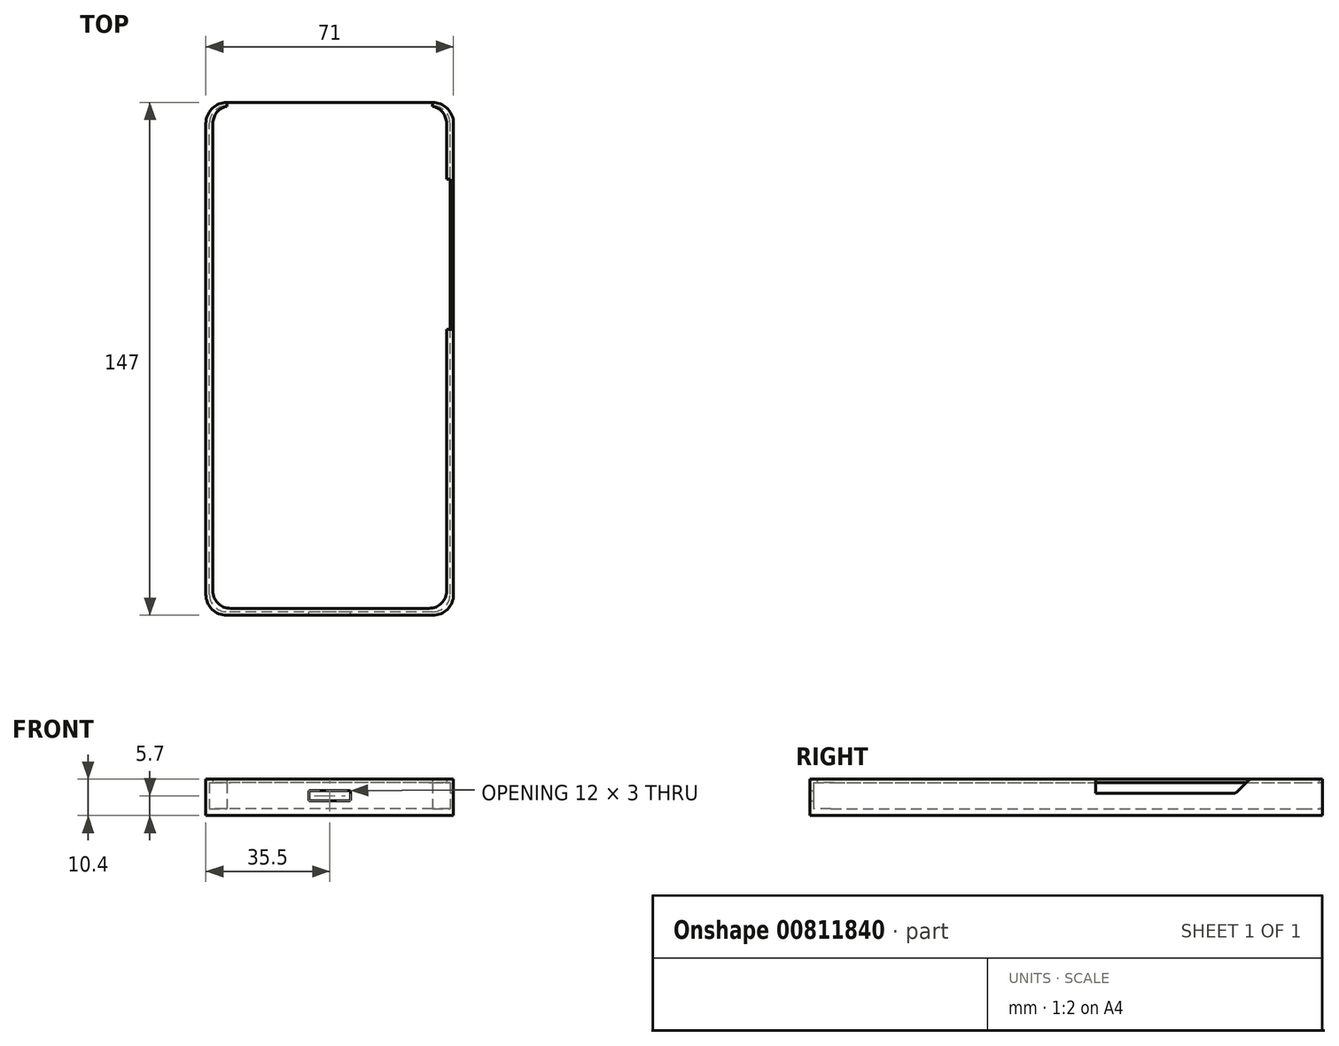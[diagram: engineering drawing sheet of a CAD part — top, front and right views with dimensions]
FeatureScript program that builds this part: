
annotation { "Feature Type Name" : "Feature", "Feature Type Description" : "" }
export const myFeature = defineFeature(function(context is Context, id is Id, definition is map)
    precondition{}
    {
        {
            var Q0;
            Q0=qCreatedBy(makeId("Top.planeOp"),FACE);
            var sketch = newSketch(context, id + "F0", { "sketchPlane" : qUnion([Q0])});
            skLineSegment(sketch, "E0.bottom", {"start": v(29.5, -72.5) * mm, "end": v(-29.5, -72.5) * mm});
            skLineSegment(sketch, "E0.top", {"start": v(29.5, 72.5) * mm, "end": v(-29.5, 72.5) * mm});
            skLineSegment(sketch, "E0.left", {"start": v(34.5, -67.5) * mm, "end": v(34.5, 67.5) * mm});
            skLineSegment(sketch, "E0.right", {"start": v(-34.5, -67.5) * mm, "end": v(-34.5, 67.5) * mm});
            skPoint(sketch, "E0.middle", {"position": v(0, 0) * mm});
            skLineSegment(sketch, "E1.bottom", {"start": v(29.5, -73.5) * mm, "end": v(-29.5, -73.5) * mm});
            skLineSegment(sketch, "E1.top", {"start": v(29.5, 73.5) * mm, "end": v(-29.5, 73.5) * mm});
            skLineSegment(sketch, "E1.left", {"start": v(35.5, -67.5) * mm, "end": v(35.5, 67.5) * mm});
            skLineSegment(sketch, "E1.right", {"start": v(-35.5, -67.5) * mm, "end": v(-35.5, 67.5) * mm});
            skPoint(sketch, "E2.visualSharp", {"position": v(-34.5, 72.5) * mm});
            skArc(sketch, "E2.filletArc", {"start": v(-29.5, 72.5) * mm, "mid": v(-33.04, 71.04) * mm, "end": v(-34.5, 67.5) * mm});
            skPoint(sketch, "E3.visualSharp", {"position": v(-34.5, -72.5) * mm});
            skArc(sketch, "E3.filletArc", {"start": v(-34.5, -67.5) * mm, "mid": v(-33.04, -71.04) * mm, "end": v(-29.5, -72.5) * mm});
            skPoint(sketch, "E4.visualSharp", {"position": v(34.5, -72.5) * mm});
            skArc(sketch, "E4.filletArc", {"start": v(29.5, -72.5) * mm, "mid": v(33.04, -71.04) * mm, "end": v(34.5, -67.5) * mm});
            skPoint(sketch, "E5.visualSharp", {"position": v(34.5, 72.5) * mm});
            skArc(sketch, "E5.filletArc", {"start": v(34.5, 67.5) * mm, "mid": v(33.04, 71.04) * mm, "end": v(29.5, 72.5) * mm});
            skPoint(sketch, "E6.visualSharp", {"position": v(-35.5, 73.5) * mm});
            skArc(sketch, "E6.filletArc", {"start": v(-29.5, 73.5) * mm, "mid": v(-33.74, 71.74) * mm, "end": v(-35.5, 67.5) * mm});
            skPoint(sketch, "E7.visualSharp", {"position": v(-35.5, -73.5) * mm});
            skArc(sketch, "E7.filletArc", {"start": v(-35.5, -67.5) * mm, "mid": v(-33.74, -71.74) * mm, "end": v(-29.5, -73.5) * mm});
            skPoint(sketch, "E8.visualSharp", {"position": v(35.5, -73.5) * mm});
            skArc(sketch, "E8.filletArc", {"start": v(29.5, -73.5) * mm, "mid": v(33.74, -71.74) * mm, "end": v(35.5, -67.5) * mm});
            skPoint(sketch, "E9.visualSharp", {"position": v(35.5, 73.5) * mm});
            skArc(sketch, "E9.filletArc", {"start": v(35.5, 67.5) * mm, "mid": v(33.74, 71.74) * mm, "end": v(29.5, 73.5) * mm});
            skSolve(sketch);
        }
        {
            var Q0;
            Q0=makeQuery(id+"F0.imprint","IMPRINT",FACE,{"disambiguationData":[TD([[makeQuery(id+"F0.imprint","IMPRINT",EDGE,{"derivedFrom":sQuery(id+"F0.wireOp",EDGE,"E0.bottom")}),-1.0]])]});
            extrude(context, id + "F1", {"entities" : qUnion([Q0]), "depth" : 1 * mm});
        }
        {
            var Q0;
            Q0=makeQuery(id+"F0.imprint","IMPRINT",FACE,{"disambiguationData":[TD([[makeQuery(id+"F0.imprint","IMPRINT",EDGE,{"derivedFrom":sQuery(id+"F0.wireOp",EDGE,"E0.bottom")}),1.0]])]});
            extrude(context, id + "F2", {"entities" : qUnion([Q0]), "operationType" : NewBodyOperationType.ADD, "depth" : (1 + 7.4) * mm});
        }
        {
            var Q0;
            Q0=makeQuery(id+"F2.opExtrude","CAP_FACE",FACE,{"disambiguationData":[OSD([sQuery(id+"F0.wireOp",EDGE,"E0.bottom"),sQuery(id+"F0.wireOp",EDGE,"E0.top"),sQuery(id+"F0.wireOp",EDGE,"E0.left"),sQuery(id+"F0.wireOp",EDGE,"E0.right"),sQuery(id+"F0.wireOp",EDGE,"E1.bottom"),sQuery(id+"F0.wireOp",EDGE,"E1.top"),sQuery(id+"F0.wireOp",EDGE,"E1.left"),sQuery(id+"F0.wireOp",EDGE,"E1.right"),sQuery(id+"F0.wireOp",EDGE,"E2.filletArc"),sQuery(id+"F0.wireOp",EDGE,"E3.filletArc"),sQuery(id+"F0.wireOp",EDGE,"E4.filletArc"),sQuery(id+"F0.wireOp",EDGE,"E5.filletArc"),sQuery(id+"F0.wireOp",EDGE,"E6.filletArc"),sQuery(id+"F0.wireOp",EDGE,"E7.filletArc"),sQuery(id+"F0.wireOp",EDGE,"E8.filletArc"),sQuery(id+"F0.wireOp",EDGE,"E9.filletArc")])],"isStart":false});
            var sketch = newSketch(context, id + "F3", { "sketchPlane" : qUnion([Q0])});
            skLineSegment(sketch, "E10.bottom", {"start": v(28.5, -71.5) * mm, "end": v(-28.5, -71.5) * mm});
            skLineSegment(sketch, "E10.top", {"start": v(28.5, 72.5) * mm, "end": v(-28.5, 72.5) * mm});
            skLineSegment(sketch, "E10.left", {"start": v(33.5, -66.5) * mm, "end": v(33.5, 67.5) * mm});
            skLineSegment(sketch, "E10.right", {"start": v(-33.5, -66.5) * mm, "end": v(-33.5, 67.5) * mm});
            skPoint(sketch, "E10.middle", {"position": v(0, 0.5) * mm});
            skPoint(sketch, "E11.visualSharp", {"position": v(-33.5, -71.5) * mm});
            skArc(sketch, "E11.filletArc", {"start": v(-33.5, -66.5) * mm, "mid": v(-32.04, -70.04) * mm, "end": v(-28.5, -71.5) * mm});
            skPoint(sketch, "E12.visualSharp", {"position": v(33.5, -71.5) * mm});
            skArc(sketch, "E12.filletArc", {"start": v(28.5, -71.5) * mm, "mid": v(32.04, -70.04) * mm, "end": v(33.5, -66.5) * mm});
            skPoint(sketch, "E13.visualSharp", {"position": v(33.5, 72.5) * mm});
            skArc(sketch, "E13.filletArc", {"start": v(33.5, 67.5) * mm, "mid": v(32.04, 71.04) * mm, "end": v(28.5, 72.5) * mm});
            skPoint(sketch, "E14.visualSharp", {"position": v(-33.5, 72.5) * mm});
            skArc(sketch, "E14.filletArc", {"start": v(-28.5, 72.5) * mm, "mid": v(-32.04, 71.04) * mm, "end": v(-33.5, 67.5) * mm});
            skSolve(sketch);
        }
        {
            var Q0;
            Q0=makeQuery(id+"F3.imprint","IMPRINT",FACE,{"disambiguationData":[TD([[makeQuery(id+"F3.imprint","IMPRINT",EDGE,{"derivedFrom":sQuery(id+"F3.wireOp",EDGE,"E10.bottom")}),1.0]])]});
            var Q1;
            Q1=makeQuery(id+"F3.imprint","IMPRINT",FACE,{"disambiguationData":[TD([[makeQuery(id+"F3.imprint","IMPRINT",EDGE,{"derivedFrom":makeQuery(id+"F2.opExtrude","CAP_EDGE",EDGE,{"disambiguationData":[OSD([sQuery(id+"F0.wireOp",EDGE,"E0.bottom")])],"isStart":false})}),1.0]])]});
            extrude(context, id + "F4", {"entities" : qUnion([Q0, Q1]), "operationType" : NewBodyOperationType.ADD, "depth" : 1 * mm});
        }
        {
            var Q0;
            Q0=makeQuery(id+"F4.boolean.opBoolean","MERGE",FACE,{"derivedFrom":[makeQuery(id+"F2.opExtrude","SWEPT_FACE",FACE,{"disambiguationData":[OSD([sQuery(id+"F0.wireOp",EDGE,"E0.top")])]}),makeQuery(id+"F4.opExtrude","SWEPT_FACE",FACE,{"disambiguationData":[OSD([sQuery(id+"F3.wireOp",EDGE,"E10.top")])]})]});
            extrude(context, id + "F5", {"entities" : qUnion([Q0]), "operationType" : NewBodyOperationType.REMOVE, "endBound" : BoundingType.THROUGH_ALL, "oppositeDirection" : true, "depth" : 25 * mm});
        }
        {
            var Q0;
            {var subQ2=sQuery(id+"F0.wireOp",EDGE,"E0.top");var subQ3=sQuery(id+"F3.wireOp",EDGE,"E14.filletArc");var subQ9=sQuery(id+"F3.wireOp",EDGE,"E10.top");var subQ16=sQuery(id+"F0.wireOp",EDGE,"E1.top");Q0=makeQuery(id+"F5.boolean.opBoolean","SPLIT",FACE,{"disambiguationData":[TD([makeQuery(id+"F5.opExtrude","SWEPT_FACE",FACE,{"disambiguationData":[OSD([subQ2,subQ9,subQ3])]})])],"derivedFrom":makeQuery(id+"F4.boolean.opBoolean","MERGE",FACE,{"derivedFrom":[makeQuery(id+"F2.opExtrude","SWEPT_FACE",FACE,{"disambiguationData":[OSD([subQ16])]}),makeQuery(id+"F4.opExtrude","SWEPT_FACE",FACE,{"disambiguationData":[OSD([subQ16])]})]})});}
            var Q1;
            {var subQ2=sQuery(id+"F3.wireOp",EDGE,"E13.filletArc");var subQ7=sQuery(id+"F3.wireOp",EDGE,"E10.top");var subQ14=sQuery(id+"F0.wireOp",EDGE,"E1.top");var subQ17=sQuery(id+"F0.wireOp",EDGE,"E0.top");Q1=makeQuery(id+"F5.boolean.opBoolean","SPLIT",FACE,{"disambiguationData":[TD([makeQuery(id+"F5.opExtrude","SWEPT_FACE",FACE,{"disambiguationData":[OSD([subQ17,subQ7,subQ2])]})])],"derivedFrom":makeQuery(id+"F4.boolean.opBoolean","MERGE",FACE,{"derivedFrom":[makeQuery(id+"F2.opExtrude","SWEPT_FACE",FACE,{"disambiguationData":[OSD([subQ14])]}),makeQuery(id+"F4.opExtrude","SWEPT_FACE",FACE,{"disambiguationData":[OSD([subQ14])]})]})});}
            extrude(context, id + "F6", {"entities" : qUnion([Q0, Q1]), "operationType" : NewBodyOperationType.REMOVE, "endBound" : BoundingType.UP_TO_NEXT, "oppositeDirection" : true, "depth" : 25 * mm});
        }
        {
            var Q0;
            {var subQ0=sQuery(id+"F0.wireOp",EDGE,"E9.filletArc");var subQ1=sQuery(id+"F0.wireOp",EDGE,"E1.top");var subQ2=makeQuery(id+"F2.opExtrude","SWEPT_FACE",FACE,{"disambiguationData":[OSD([subQ0])]});var subQ3=makeQuery(id+"F4.opExtrude","SWEPT_FACE",FACE,{"disambiguationData":[OSD([subQ0])]});var subQ4=sQuery(id+"F0.wireOp",EDGE,"E5.filletArc");var subQ5=sQuery(id+"F0.wireOp",EDGE,"E0.top");var subQ6=makeQuery(id+"F5.opExtrude","SWEPT_FACE",FACE,{"disambiguationData":[OSD([subQ5,subQ4])]});var subQ7=makeQuery(id+"F4.boolean.opBoolean","MERGE",EDGE,{"derivedFrom":[makeQuery(id+"F2.opExtrude","SWEPT_EDGE",EDGE,{"disambiguationData":[OSD([subQ1,subQ0])]}),makeQuery(id+"F4.opExtrude","SWEPT_EDGE",EDGE,{"disambiguationData":[OSD([subQ1,subQ0])]})]});var subQ22=makeQuery(id+"F2.opExtrude","SWEPT_FACE",FACE,{"disambiguationData":[OSD([subQ1])]});var subQ24=makeQuery(id+"F4.opExtrude","SWEPT_FACE",FACE,{"disambiguationData":[OSD([subQ1])]});var subQ27=makeQuery(id+"F2.opExtrude","CAP_EDGE",EDGE,{"disambiguationData":[OSD([subQ5])],"isStart":false});Q0=makeQuery(id+"F6.boolean.opBoolean","MERGE",EDGE,{"derivedFrom":[makeQuery(id+"F5.boolean.opBoolean","SPLIT",EDGE,{"disambiguationData":[topologyDisambiguationEdgeConnected([subQ22,subQ2,subQ24,subQ3]),TD([makeQuery(id+"F5.opExtrude","SWEPT_FACE",FACE,{"disambiguationData":[OSD([subQ5]),TDD([makeQuery(id+"F4.boolean.opBoolean","SPLIT",EDGE,{"disambiguationData":[TD([makeQuery(id+"F2.opExtrude","SWEPT_FACE",FACE,{"disambiguationData":[OSD([subQ4])]})])],"derivedFrom":subQ27})])]})])],"derivedFrom":subQ7}),makeQuery(id+"F5.boolean.opBoolean","SPLIT",EDGE,{"disambiguationData":[topologyDisambiguationEdgeConnected([subQ2,subQ3,subQ6])],"derivedFrom":subQ7}),makeQuery(id+"F6.opExtrude","CAP_EDGE",EDGE,{"disambiguationData":[OSD([subQ1,subQ0])],"isStart":true})]});}
            var Q1;
            {var subQ0=sQuery(id+"F0.wireOp",EDGE,"E6.filletArc");var subQ1=sQuery(id+"F0.wireOp",EDGE,"E1.top");var subQ2=makeQuery(id+"F2.opExtrude","SWEPT_FACE",FACE,{"disambiguationData":[OSD([subQ0])]});var subQ3=sQuery(id+"F0.wireOp",EDGE,"E2.filletArc");var subQ4=sQuery(id+"F0.wireOp",EDGE,"E0.top");var subQ5=makeQuery(id+"F5.opExtrude","SWEPT_FACE",FACE,{"disambiguationData":[OSD([subQ4,subQ3])]});var subQ6=makeQuery(id+"F4.opExtrude","SWEPT_FACE",FACE,{"disambiguationData":[OSD([subQ0])]});var subQ7=makeQuery(id+"F4.boolean.opBoolean","MERGE",EDGE,{"derivedFrom":[makeQuery(id+"F2.opExtrude","SWEPT_EDGE",EDGE,{"disambiguationData":[OSD([subQ1,subQ0])]}),makeQuery(id+"F4.opExtrude","SWEPT_EDGE",EDGE,{"disambiguationData":[OSD([subQ1,subQ0])]})]});var subQ22=makeQuery(id+"F2.opExtrude","SWEPT_FACE",FACE,{"disambiguationData":[OSD([subQ1])]});var subQ24=makeQuery(id+"F4.opExtrude","SWEPT_FACE",FACE,{"disambiguationData":[OSD([subQ1])]});var subQ27=makeQuery(id+"F2.opExtrude","CAP_EDGE",EDGE,{"disambiguationData":[OSD([subQ4])],"isStart":false});Q1=makeQuery(id+"F6.boolean.opBoolean","MERGE",EDGE,{"derivedFrom":[makeQuery(id+"F5.boolean.opBoolean","SPLIT",EDGE,{"disambiguationData":[topologyDisambiguationEdgeConnected([subQ22,subQ2,subQ24,subQ6]),TD([makeQuery(id+"F5.opExtrude","SWEPT_FACE",FACE,{"disambiguationData":[OSD([subQ4]),TDD([makeQuery(id+"F4.boolean.opBoolean","SPLIT",EDGE,{"disambiguationData":[TD([makeQuery(id+"F2.opExtrude","SWEPT_FACE",FACE,{"disambiguationData":[OSD([sQuery(id+"F0.wireOp",EDGE,"E5.filletArc")])]})])],"derivedFrom":subQ27})])]})])],"derivedFrom":subQ7}),makeQuery(id+"F5.boolean.opBoolean","SPLIT",EDGE,{"disambiguationData":[topologyDisambiguationEdgeConnected([subQ2,subQ6,subQ5])],"derivedFrom":subQ7}),makeQuery(id+"F6.opExtrude","CAP_EDGE",EDGE,{"disambiguationData":[OSD([subQ1,subQ0])],"isStart":true})]});}
            var Q2;
            {var subQ0=sQuery(id+"F0.wireOp",EDGE,"E2.filletArc");var subQ1=sQuery(id+"F0.wireOp",EDGE,"E0.top");Q2=makeQuery(id+"F5.boolean.opBoolean","MERGE",EDGE,{"derivedFrom":[makeQuery(id+"F2.opExtrude","SWEPT_EDGE",EDGE,{"disambiguationData":[OSD([subQ1,subQ0])]}),makeQuery(id+"F5.opExtrude","CAP_EDGE",EDGE,{"disambiguationData":[OSD([subQ1,subQ0])],"isStart":true})]});}
            var Q3;
            {var subQ0=sQuery(id+"F0.wireOp",EDGE,"E5.filletArc");var subQ1=sQuery(id+"F0.wireOp",EDGE,"E0.top");Q3=makeQuery(id+"F5.boolean.opBoolean","MERGE",EDGE,{"derivedFrom":[makeQuery(id+"F2.opExtrude","SWEPT_EDGE",EDGE,{"disambiguationData":[OSD([subQ1,subQ0])]}),makeQuery(id+"F5.opExtrude","CAP_EDGE",EDGE,{"disambiguationData":[OSD([subQ1,subQ0])],"isStart":true})]});}
            fillet(context, id + "F7", {"entities" : qUnion([Q0, Q1, Q2, Q3]), "radius" : 0.5 * mm, "tangentPropagation" : true, "allowEdgeOverflow" : false});
        }
        {
            var Q0;
            Q0=makeQuery(id+"F2.opExtrude","SWEPT_FACE",FACE,{"disambiguationData":[OSD([sQuery(id+"F0.wireOp",EDGE,"E0.bottom")])]});
            var sketch = newSketch(context, id + "F8", { "sketchPlane" : qUnion([Q0])});
            skLineSegment(sketch, "E15", {"start": v(0, 1) * mm, "end": v(0, 8.4) * mm, "construction": true});
            skLineSegment(sketch, "E16.bottom", {"start": v(-6, 6.2) * mm, "end": v(6, 6.2) * mm});
            skLineSegment(sketch, "E16.top", {"start": v(-6, 3.2) * mm, "end": v(6, 3.2) * mm});
            skLineSegment(sketch, "E16.left", {"start": v(-6, 6.2) * mm, "end": v(-6, 3.2) * mm});
            skLineSegment(sketch, "E16.right", {"start": v(6, 6.2) * mm, "end": v(6, 3.2) * mm});
            skPoint(sketch, "E16.middle", {"position": v(0, 4.7) * mm});
            skSolve(sketch);
        }
        {
            var Q0;
            Q0=makeQuery(id+"F8.imprint","IMPRINT",FACE,{"disambiguationData":[TD([[makeQuery(id+"F8.imprint","IMPRINT",EDGE,{"derivedFrom":sQuery(id+"F8.wireOp",EDGE,"E16.bottom")}),-1.0]])]});
            extrude(context, id + "F9", {"entities" : qUnion([Q0]), "operationType" : NewBodyOperationType.REMOVE, "endBound" : BoundingType.UP_TO_NEXT, "oppositeDirection" : true, "depth" : 25 * mm});
        }
        {
            var Q0;
            Q0=makeQuery(id+"F9.boolean.opBoolean","COPY",EDGE,{"derivedFrom":makeQuery(id+"F9.opExtrude","SWEPT_EDGE",EDGE,{"disambiguationData":[OSD([sQuery(id+"F8.wireOp",EDGE,"E16.top"),sQuery(id+"F8.wireOp",EDGE,"E16.right")])]})});
            var Q1;
            Q1=makeQuery(id+"F9.boolean.opBoolean","COPY",EDGE,{"derivedFrom":makeQuery(id+"F9.opExtrude","SWEPT_EDGE",EDGE,{"disambiguationData":[OSD([sQuery(id+"F8.wireOp",EDGE,"E16.top"),sQuery(id+"F8.wireOp",EDGE,"E16.left")])]})});
            var Q2;
            Q2=makeQuery(id+"F9.boolean.opBoolean","COPY",EDGE,{"derivedFrom":makeQuery(id+"F9.opExtrude","SWEPT_EDGE",EDGE,{"disambiguationData":[OSD([sQuery(id+"F8.wireOp",EDGE,"E16.bottom"),sQuery(id+"F8.wireOp",EDGE,"E16.right")])]})});
            var Q3;
            Q3=makeQuery(id+"F9.boolean.opBoolean","COPY",EDGE,{"derivedFrom":makeQuery(id+"F9.opExtrude","SWEPT_EDGE",EDGE,{"disambiguationData":[OSD([sQuery(id+"F8.wireOp",EDGE,"E16.bottom"),sQuery(id+"F8.wireOp",EDGE,"E16.left")])]})});
            fillet(context, id + "F10", {"entities" : qUnion([Q0, Q1, Q2, Q3]), "radius" : 0.5 * mm, "tangentPropagation" : true, "allowEdgeOverflow" : false});
        }
        {
            var Q0;
            {var subQ0=sQuery(id+"F0.wireOp",EDGE,"E1.left");Q0=makeQuery(id+"F4.boolean.opBoolean","MERGE",FACE,{"derivedFrom":[makeQuery(id+"F2.opExtrude","SWEPT_FACE",FACE,{"disambiguationData":[OSD([subQ0])]}),makeQuery(id+"F4.opExtrude","SWEPT_FACE",FACE,{"disambiguationData":[OSD([subQ0])]})]});}
            var sketch = newSketch(context, id + "F11", { "sketchPlane" : qUnion([Q0])});
            skLineSegment(sketch, "E17.bottom", {"start": v(48.48, 9.4) * mm, "end": v(8.48, 9.4) * mm});
            skLineSegment(sketch, "E17.top", {"start": v(48.48, 5.4) * mm, "end": v(8.48, 5.4) * mm});
            skLineSegment(sketch, "E17.left", {"start": v(48.48, 9.4) * mm, "end": v(48.48, 5.4) * mm});
            skLineSegment(sketch, "E17.right", {"start": v(8.48, 9.4) * mm, "end": v(8.48, 5.4) * mm});
            skSolve(sketch);
        }
        {
            var Q0;
            Q0=qSketchRegion(id+"F11",true);
            extrude(context, id + "F12", {"entities" : qUnion([Q0]), "operationType" : NewBodyOperationType.REMOVE, "endBound" : BoundingType.UP_TO_NEXT, "oppositeDirection" : true, "depth" : 25 * mm});
        }
        {
            var Q0;
            Q0=makeQuery(id+"F12.boolean.opBoolean","COPY",EDGE,{"derivedFrom":makeQuery(id+"F12.opExtrude","SWEPT_EDGE",EDGE,{"disambiguationData":[OSD([sQuery(id+"F0.wireOp",EDGE,"E1.left"),sQuery(id+"F11.wireOp",EDGE,"E17.bottom"),sQuery(id+"F11.wireOp",EDGE,"E17.left")])]})});
            var Q1;
            Q1=makeQuery(id+"F12.boolean.opBoolean","COPY",EDGE,{"derivedFrom":makeQuery(id+"F12.opExtrude","SWEPT_EDGE",EDGE,{"disambiguationData":[OSD([sQuery(id+"F0.wireOp",EDGE,"E1.left"),sQuery(id+"F11.wireOp",EDGE,"E17.bottom"),sQuery(id+"F11.wireOp",EDGE,"E17.right")])]})});
            chamfer(context, id + "F13", {"entities" : qUnion([Q0, Q1]), "width" : 4 * mm, "tangentPropagation" : true});
        }
        {
            var Q0;
            Q0=makeQuery(id+"F13.opChamfer","BLEND_EDGE",EDGE,{"blendedFrom":[makeQuery(id+"F12.boolean.opBoolean","COPY",EDGE,{"derivedFrom":makeQuery(id+"F12.opExtrude","SWEPT_EDGE",EDGE,{"disambiguationData":[OSD([sQuery(id+"F0.wireOp",EDGE,"E1.left"),sQuery(id+"F11.wireOp",EDGE,"E17.bottom"),sQuery(id+"F11.wireOp",EDGE,"E17.left")])]})}),makeQuery(id+"F12.boolean.opBoolean","COPY",FACE,{"derivedFrom":makeQuery(id+"F12.opExtrude","SWEPT_FACE",FACE,{"disambiguationData":[OSD([sQuery(id+"F11.wireOp",EDGE,"E17.top")])]})})],"blendedInto":[makeQuery(id+"F12.boolean.opBoolean","COPY",FACE,{"derivedFrom":makeQuery(id+"F12.opExtrude","SWEPT_FACE",FACE,{"disambiguationData":[OSD([sQuery(id+"F11.wireOp",EDGE,"E17.top")])]})})]});
            var Q1;
            Q1=makeQuery(id+"F13.opChamfer","BLEND_EDGE",EDGE,{"blendedFrom":[makeQuery(id+"F12.boolean.opBoolean","COPY",EDGE,{"derivedFrom":makeQuery(id+"F12.opExtrude","SWEPT_EDGE",EDGE,{"disambiguationData":[OSD([sQuery(id+"F0.wireOp",EDGE,"E1.left"),sQuery(id+"F11.wireOp",EDGE,"E17.bottom"),sQuery(id+"F11.wireOp",EDGE,"E17.right")])]})}),makeQuery(id+"F12.boolean.opBoolean","COPY",FACE,{"derivedFrom":makeQuery(id+"F12.opExtrude","SWEPT_FACE",FACE,{"disambiguationData":[OSD([sQuery(id+"F11.wireOp",EDGE,"E17.top")])]})})],"blendedInto":[makeQuery(id+"F12.boolean.opBoolean","COPY",FACE,{"derivedFrom":makeQuery(id+"F12.opExtrude","SWEPT_FACE",FACE,{"disambiguationData":[OSD([sQuery(id+"F11.wireOp",EDGE,"E17.top")])]})})]});
            fillet(context, id + "F14", {"entities" : qUnion([Q0, Q1]), "radius" : 1 * mm, "tangentPropagation" : true, "allowEdgeOverflow" : false});
        }
        {
            var Q0;
            {var subQ0=sQuery(id+"F3.wireOp",EDGE,"E13.filletArc");var subQ1=sQuery(id+"F0.wireOp",EDGE,"E9.filletArc");var subQ2=sQuery(id+"F0.wireOp",EDGE,"E1.left");var subQ3=sQuery(id+"F3.wireOp",EDGE,"E10.left");var subQ4=sQuery(id+"F0.wireOp",EDGE,"E1.top");var subQ5=sQuery(id+"F11.wireOp",EDGE,"E17.left");Q0=makeQuery(id+"F13.opChamfer","BLEND_EDGE",EDGE,{"blendedFrom":[makeQuery(id+"F12.boolean.opBoolean","COPY",EDGE,{"derivedFrom":makeQuery(id+"F12.opExtrude","SWEPT_EDGE",EDGE,{"disambiguationData":[OSD([subQ2,sQuery(id+"F11.wireOp",EDGE,"E17.bottom"),subQ5])]})}),makeQuery(id+"F12.boolean.opBoolean","SPLIT",FACE,{"disambiguationData":[TD([makeQuery(id+"F2.opExtrude","SWEPT_FACE",FACE,{"disambiguationData":[OSD([subQ1])]})])],"derivedFrom":makeQuery(id+"F4.opExtrude","CAP_FACE",FACE,{"disambiguationData":[OSD([sQuery(id+"F0.wireOp",EDGE,"E1.bottom"),subQ4,subQ2,sQuery(id+"F0.wireOp",EDGE,"E1.right"),sQuery(id+"F0.wireOp",EDGE,"E6.filletArc"),sQuery(id+"F0.wireOp",EDGE,"E7.filletArc"),sQuery(id+"F0.wireOp",EDGE,"E8.filletArc"),subQ1,sQuery(id+"F3.wireOp",EDGE,"E10.bottom"),sQuery(id+"F3.wireOp",EDGE,"E10.top"),subQ3,sQuery(id+"F3.wireOp",EDGE,"E10.right"),sQuery(id+"F3.wireOp",EDGE,"E11.filletArc"),sQuery(id+"F3.wireOp",EDGE,"E12.filletArc"),subQ0,sQuery(id+"F3.wireOp",EDGE,"E14.filletArc")])],"isStart":false})})],"blendedInto":[makeQuery(id+"F12.boolean.opBoolean","SPLIT",FACE,{"disambiguationData":[TD([makeQuery(id+"F2.opExtrude","SWEPT_FACE",FACE,{"disambiguationData":[OSD([subQ1])]})])],"derivedFrom":makeQuery(id+"F4.opExtrude","CAP_FACE",FACE,{"disambiguationData":[OSD([sQuery(id+"F0.wireOp",EDGE,"E1.bottom"),subQ4,subQ2,sQuery(id+"F0.wireOp",EDGE,"E1.right"),sQuery(id+"F0.wireOp",EDGE,"E6.filletArc"),sQuery(id+"F0.wireOp",EDGE,"E7.filletArc"),sQuery(id+"F0.wireOp",EDGE,"E8.filletArc"),subQ1,sQuery(id+"F3.wireOp",EDGE,"E10.bottom"),sQuery(id+"F3.wireOp",EDGE,"E10.top"),subQ3,sQuery(id+"F3.wireOp",EDGE,"E10.right"),sQuery(id+"F3.wireOp",EDGE,"E11.filletArc"),sQuery(id+"F3.wireOp",EDGE,"E12.filletArc"),subQ0,sQuery(id+"F3.wireOp",EDGE,"E14.filletArc")])],"isStart":false})})]});}
            var Q1;
            {var subQ0=sQuery(id+"F3.wireOp",EDGE,"E11.filletArc");var subQ1=sQuery(id+"F0.wireOp",EDGE,"E6.filletArc");var subQ2=sQuery(id+"F0.wireOp",EDGE,"E1.top");var subQ3=sQuery(id+"F3.wireOp",EDGE,"E10.right");var subQ4=sQuery(id+"F3.wireOp",EDGE,"E10.bottom");var subQ5=sQuery(id+"F0.wireOp",EDGE,"E8.filletArc");var subQ6=sQuery(id+"F0.wireOp",EDGE,"E7.filletArc");var subQ7=sQuery(id+"F0.wireOp",EDGE,"E1.bottom");var subQ8=sQuery(id+"F0.wireOp",EDGE,"E1.left");var subQ9=sQuery(id+"F3.wireOp",EDGE,"E10.left");var subQ10=sQuery(id+"F11.wireOp",EDGE,"E17.right");var subQ11=sQuery(id+"F0.wireOp",EDGE,"E1.right");var subQ12=sQuery(id+"F3.wireOp",EDGE,"E12.filletArc");var subQ13=sQuery(id+"F3.wireOp",EDGE,"E14.filletArc");Q1=makeQuery(id+"F13.opChamfer","BLEND_EDGE",EDGE,{"blendedFrom":[makeQuery(id+"F12.boolean.opBoolean","COPY",EDGE,{"derivedFrom":makeQuery(id+"F12.opExtrude","SWEPT_EDGE",EDGE,{"disambiguationData":[OSD([subQ8,sQuery(id+"F11.wireOp",EDGE,"E17.bottom"),subQ10])]})}),makeQuery(id+"F12.boolean.opBoolean","SPLIT",FACE,{"disambiguationData":[TD([makeQuery(id+"F2.opExtrude","SWEPT_FACE",FACE,{"disambiguationData":[OSD([subQ7])]})])],"derivedFrom":makeQuery(id+"F4.opExtrude","CAP_FACE",FACE,{"disambiguationData":[OSD([subQ7,subQ2,subQ8,subQ11,subQ1,subQ6,subQ5,sQuery(id+"F0.wireOp",EDGE,"E9.filletArc"),subQ4,sQuery(id+"F3.wireOp",EDGE,"E10.top"),subQ9,subQ3,subQ0,subQ12,sQuery(id+"F3.wireOp",EDGE,"E13.filletArc"),subQ13])],"isStart":false})})],"blendedInto":[makeQuery(id+"F12.boolean.opBoolean","SPLIT",FACE,{"disambiguationData":[TD([makeQuery(id+"F2.opExtrude","SWEPT_FACE",FACE,{"disambiguationData":[OSD([subQ7])]})])],"derivedFrom":makeQuery(id+"F4.opExtrude","CAP_FACE",FACE,{"disambiguationData":[OSD([subQ7,subQ2,subQ8,subQ11,subQ1,subQ6,subQ5,sQuery(id+"F0.wireOp",EDGE,"E9.filletArc"),subQ4,sQuery(id+"F3.wireOp",EDGE,"E10.top"),subQ9,subQ3,subQ0,subQ12,sQuery(id+"F3.wireOp",EDGE,"E13.filletArc"),subQ13])],"isStart":false})})]});}
            fillet(context, id + "F15", {"entities" : qUnion([Q0, Q1]), "radius" : 1 * mm, "tangentPropagation" : true, "allowEdgeOverflow" : false});
        }
        {
            var Q0;
            {var subQ0=sQuery(id+"F0.wireOp",EDGE,"E5.filletArc");var subQ1=sQuery(id+"F0.wireOp",EDGE,"E4.filletArc");var subQ2=sQuery(id+"F0.wireOp",EDGE,"E3.filletArc");var subQ3=sQuery(id+"F0.wireOp",EDGE,"E2.filletArc");var subQ4=sQuery(id+"F0.wireOp",EDGE,"E0.right");var subQ5=sQuery(id+"F0.wireOp",EDGE,"E0.left");var subQ6=sQuery(id+"F0.wireOp",EDGE,"E0.top");var subQ7=sQuery(id+"F0.wireOp",EDGE,"E0.bottom");Q0=makeQuery(id+"F2.boolean.opBoolean","MERGE",FACE,{"derivedFrom":[makeQuery(id+"F1.opExtrude","CAP_FACE",FACE,{"disambiguationData":[OSD([subQ7,subQ6,subQ5,subQ4,subQ3,subQ2,subQ1,subQ0])],"isStart":true}),makeQuery(id+"F2.opExtrude","CAP_FACE",FACE,{"disambiguationData":[OSD([subQ7,subQ6,subQ5,subQ4,sQuery(id+"F0.wireOp",EDGE,"E1.bottom"),sQuery(id+"F0.wireOp",EDGE,"E1.top"),sQuery(id+"F0.wireOp",EDGE,"E1.left"),sQuery(id+"F0.wireOp",EDGE,"E1.right"),subQ3,subQ2,subQ1,subQ0,sQuery(id+"F0.wireOp",EDGE,"E6.filletArc"),sQuery(id+"F0.wireOp",EDGE,"E7.filletArc"),sQuery(id+"F0.wireOp",EDGE,"E8.filletArc"),sQuery(id+"F0.wireOp",EDGE,"E9.filletArc")])],"isStart":true})]});}
            extrude(context, id + "F16", {"entities" : qUnion([Q0]), "operationType" : NewBodyOperationType.ADD, "depth" : 1 * mm, "offsetDistance" : 25 * mm});
        }
    });
